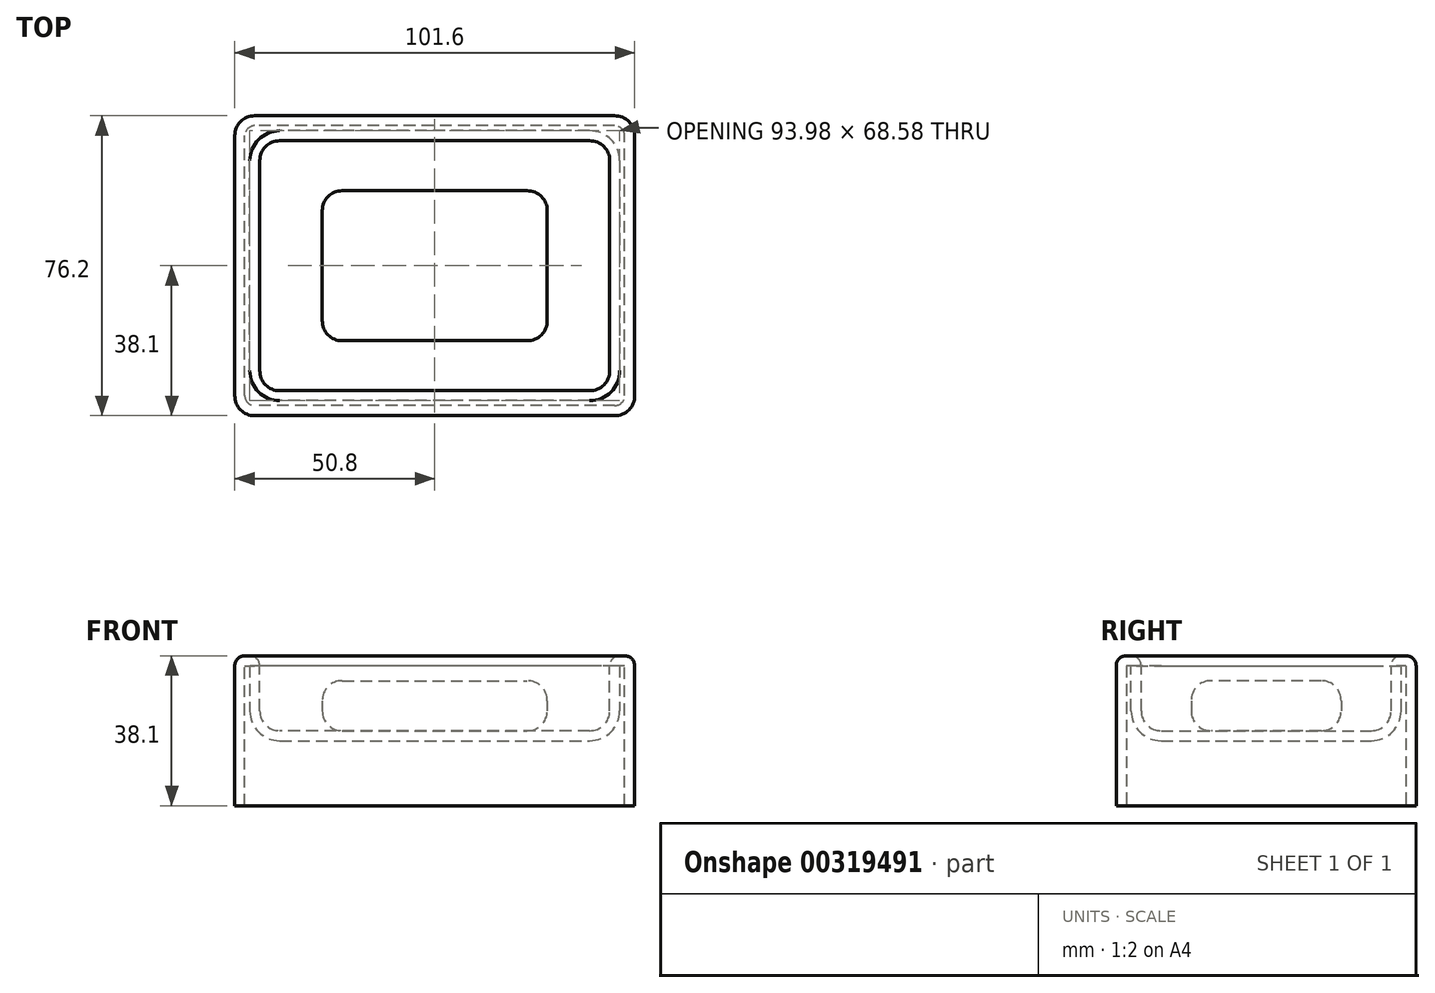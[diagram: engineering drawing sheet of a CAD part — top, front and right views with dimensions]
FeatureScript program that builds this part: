
annotation { "Feature Type Name" : "Feature", "Feature Type Description" : "" }
export const myFeature = defineFeature(function(context is Context, id is Id, definition is map)
    precondition{}
    {
        {
            var Q0;
            Q0=qCreatedBy(makeId("Top.planeOp"),FACE);
            var sketch = newSketch(context, id + "F0", { "sketchPlane" : qUnion([Q0])});
            skLineSegment(sketch, "E0.bottom", {"start": v(50.8, -38.1) * mm, "end": v(-50.8, -38.1) * mm});
            skLineSegment(sketch, "E0.top", {"start": v(50.8, 38.1) * mm, "end": v(-50.8, 38.1) * mm});
            skLineSegment(sketch, "E0.left", {"start": v(50.8, -38.1) * mm, "end": v(50.8, 38.1) * mm});
            skLineSegment(sketch, "E0.right", {"start": v(-50.8, -38.1) * mm, "end": v(-50.8, 38.1) * mm});
            skPoint(sketch, "E0.middle", {"position": v(0, 0) * mm});
            skSolve(sketch);
        }
        {
            var Q0;
            Q0=makeQuery(id+"F0.imprint","IMPRINT",FACE,{"disambiguationData":[TD([[makeQuery(id+"F0.imprint","IMPRINT",EDGE,{"derivedFrom":sQuery(id+"F0.wireOp",EDGE,"E0.bottom")}),-1.0]])]});
            extrude(context, id + "F1", {"entities" : qUnion([Q0]), "depth" : 38.1 * mm});
        }
        {
            var Q0;
            Q0=makeQuery(id+"F1.opExtrude","CAP_FACE",FACE,{"disambiguationData":[OSD([sQuery(id+"F0.wireOp",EDGE,"E0.bottom"),sQuery(id+"F0.wireOp",EDGE,"E0.top"),sQuery(id+"F0.wireOp",EDGE,"E0.left"),sQuery(id+"F0.wireOp",EDGE,"E0.right")])],"isStart":false});
            var sketch = newSketch(context, id + "F2", { "sketchPlane" : qUnion([Q0])});
            skLineSegment(sketch, "E1.bottom", {"start": v(44.45, -31.75) * mm, "end": v(-44.45, -31.75) * mm});
            skLineSegment(sketch, "E1.top", {"start": v(44.45, 31.75) * mm, "end": v(-44.45, 31.75) * mm});
            skLineSegment(sketch, "E1.left", {"start": v(44.45, -31.75) * mm, "end": v(44.45, 31.75) * mm});
            skLineSegment(sketch, "E1.right", {"start": v(-44.45, -31.75) * mm, "end": v(-44.45, 31.75) * mm});
            skPoint(sketch, "E1.middle", {"position": v(0, 0) * mm});
            skSolve(sketch);
        }
        {
            var Q0;
            Q0=makeQuery(id+"F2.imprint","IMPRINT",FACE,{"disambiguationData":[TD([[makeQuery(id+"F2.imprint","IMPRINT",EDGE,{"derivedFrom":sQuery(id+"F2.wireOp",EDGE,"E1.bottom")}),-1.0]])]});
            extrude(context, id + "F3", {"entities" : qUnion([Q0]), "operationType" : NewBodyOperationType.REMOVE, "oppositeDirection" : true, "depth" : 19.05 * mm});
        }
        {
            var Q0;
            Q0=makeQuery(id+"F3.boolean.opBoolean","COPY",FACE,{"derivedFrom":makeQuery(id+"F3.opExtrude","CAP_FACE",FACE,{"disambiguationData":[OSD([sQuery(id+"F2.wireOp",EDGE,"E1.bottom"),sQuery(id+"F2.wireOp",EDGE,"E1.top"),sQuery(id+"F2.wireOp",EDGE,"E1.left"),sQuery(id+"F2.wireOp",EDGE,"E1.right")])],"isStart":false})});
            var Q1;
            Q1=makeQuery(id+"F3.boolean.opBoolean","COPY",EDGE,{"derivedFrom":makeQuery(id+"F3.opExtrude","SWEPT_EDGE",EDGE,{"disambiguationData":[OSD([sQuery(id+"F2.wireOp",EDGE,"E1.bottom"),sQuery(id+"F2.wireOp",EDGE,"E1.right")])]})});
            var Q2;
            Q2=makeQuery(id+"F3.boolean.opBoolean","COPY",EDGE,{"derivedFrom":makeQuery(id+"F3.opExtrude","SWEPT_EDGE",EDGE,{"disambiguationData":[OSD([sQuery(id+"F2.wireOp",EDGE,"E1.top"),sQuery(id+"F2.wireOp",EDGE,"E1.right")])]})});
            var Q3;
            Q3=makeQuery(id+"F3.boolean.opBoolean","COPY",EDGE,{"derivedFrom":makeQuery(id+"F3.opExtrude","SWEPT_EDGE",EDGE,{"disambiguationData":[OSD([sQuery(id+"F2.wireOp",EDGE,"E1.top"),sQuery(id+"F2.wireOp",EDGE,"E1.left")])]})});
            var Q4;
            Q4=makeQuery(id+"F3.boolean.opBoolean","COPY",EDGE,{"derivedFrom":makeQuery(id+"F3.opExtrude","SWEPT_EDGE",EDGE,{"disambiguationData":[OSD([sQuery(id+"F2.wireOp",EDGE,"E1.bottom"),sQuery(id+"F2.wireOp",EDGE,"E1.left")])]})});
            var Q5;
            Q5=makeQuery(id+"F1.opExtrude","SWEPT_EDGE",EDGE,{"disambiguationData":[OSD([sQuery(id+"F0.wireOp",EDGE,"E0.bottom"),sQuery(id+"F0.wireOp",EDGE,"E0.left")])]});
            var Q6;
            Q6=makeQuery(id+"F1.opExtrude","SWEPT_EDGE",EDGE,{"disambiguationData":[OSD([sQuery(id+"F0.wireOp",EDGE,"E0.top"),sQuery(id+"F0.wireOp",EDGE,"E0.left")])]});
            var Q7;
            Q7=makeQuery(id+"F1.opExtrude","SWEPT_EDGE",EDGE,{"disambiguationData":[OSD([sQuery(id+"F0.wireOp",EDGE,"E0.top"),sQuery(id+"F0.wireOp",EDGE,"E0.right")])]});
            var Q8;
            Q8=makeQuery(id+"F1.opExtrude","SWEPT_EDGE",EDGE,{"disambiguationData":[OSD([sQuery(id+"F0.wireOp",EDGE,"E0.bottom"),sQuery(id+"F0.wireOp",EDGE,"E0.right")])]});
            fillet(context, id + "F4", {"entities" : qUnion([Q0, Q1, Q2, Q3, Q4, Q5, Q6, Q7, Q8]), "radius" : 5.08 * mm, "tangentPropagation" : true, "allowEdgeOverflow" : false});
        }
        {
            var Q0;
            Q0=makeQuery(id+"F1.opExtrude","CAP_FACE",FACE,{"disambiguationData":[OSD([sQuery(id+"F0.wireOp",EDGE,"E0.bottom"),sQuery(id+"F0.wireOp",EDGE,"E0.top"),sQuery(id+"F0.wireOp",EDGE,"E0.left"),sQuery(id+"F0.wireOp",EDGE,"E0.right")])],"isStart":false});
            fillet(context, id + "F5", {"entities" : qUnion([Q0]), "radius" : 2.54 * mm, "tangentPropagation" : true, "allowEdgeOverflow" : false});
        }
        {
            var Q0;
            Q0=makeQuery(id+"F1.opExtrude","CAP_FACE",FACE,{"disambiguationData":[OSD([sQuery(id+"F0.wireOp",EDGE,"E0.bottom"),sQuery(id+"F0.wireOp",EDGE,"E0.top"),sQuery(id+"F0.wireOp",EDGE,"E0.left"),sQuery(id+"F0.wireOp",EDGE,"E0.right")])],"isStart":true});
            shell(context, id + "F6", {"entities" : qUnion([Q0]), "thickness" : 2.54 * mm});
        }
        {
            var Q0;
            Q0=makeQuery(id+"F3.boolean.opBoolean","COPY",FACE,{"derivedFrom":makeQuery(id+"F3.opExtrude","CAP_FACE",FACE,{"disambiguationData":[OSD([sQuery(id+"F2.wireOp",EDGE,"E1.bottom"),sQuery(id+"F2.wireOp",EDGE,"E1.top"),sQuery(id+"F2.wireOp",EDGE,"E1.left"),sQuery(id+"F2.wireOp",EDGE,"E1.right")])],"isStart":false})});
            var sketch = newSketch(context, id + "F7", { "sketchPlane" : qUnion([Q0])});
            skLineSegment(sketch, "E2.bottom", {"start": v(-28.57, 19.05) * mm, "end": v(28.58, 19.05) * mm});
            skLineSegment(sketch, "E2.top", {"start": v(-28.58, -19.05) * mm, "end": v(28.57, -19.05) * mm});
            skLineSegment(sketch, "E2.left", {"start": v(-28.57, 19.05) * mm, "end": v(-28.58, -19.05) * mm});
            skLineSegment(sketch, "E2.right", {"start": v(28.58, 19.05) * mm, "end": v(28.57, -19.05) * mm});
            skPoint(sketch, "E2.middle", {"position": v(0, 0) * mm});
            skSolve(sketch);
        }
        {
            var Q0;
            Q0=makeQuery(id+"F7.imprint","IMPRINT",FACE,{"disambiguationData":[TD([[makeQuery(id+"F7.imprint","IMPRINT",EDGE,{"derivedFrom":sQuery(id+"F7.wireOp",EDGE,"E2.bottom")}),-1.0]])]});
            extrude(context, id + "F8", {"entities" : qUnion([Q0]), "depth" : 12.7 * mm});
        }
        {
            var Q0;
            Q0=makeQuery(id+"F8.opExtrude","SWEPT_FACE",FACE,{"disambiguationData":[OSD([sQuery(id+"F7.wireOp",EDGE,"E2.left")])]});
            var Q1;
            Q1=makeQuery(id+"F8.opExtrude","SWEPT_FACE",FACE,{"disambiguationData":[OSD([sQuery(id+"F7.wireOp",EDGE,"E2.bottom")])]});
            var Q2;
            Q2=makeQuery(id+"F8.opExtrude","SWEPT_FACE",FACE,{"disambiguationData":[OSD([sQuery(id+"F7.wireOp",EDGE,"E2.right")])]});
            var Q3;
            Q3=makeQuery(id+"F8.opExtrude","SWEPT_FACE",FACE,{"disambiguationData":[OSD([sQuery(id+"F7.wireOp",EDGE,"E2.top")])]});
            fillet(context, id + "F9", {"entities" : qUnion([Q0, Q1, Q2, Q3]), "radius" : 5.08 * mm, "tangentPropagation" : true, "allowEdgeOverflow" : false});
        }
    });
